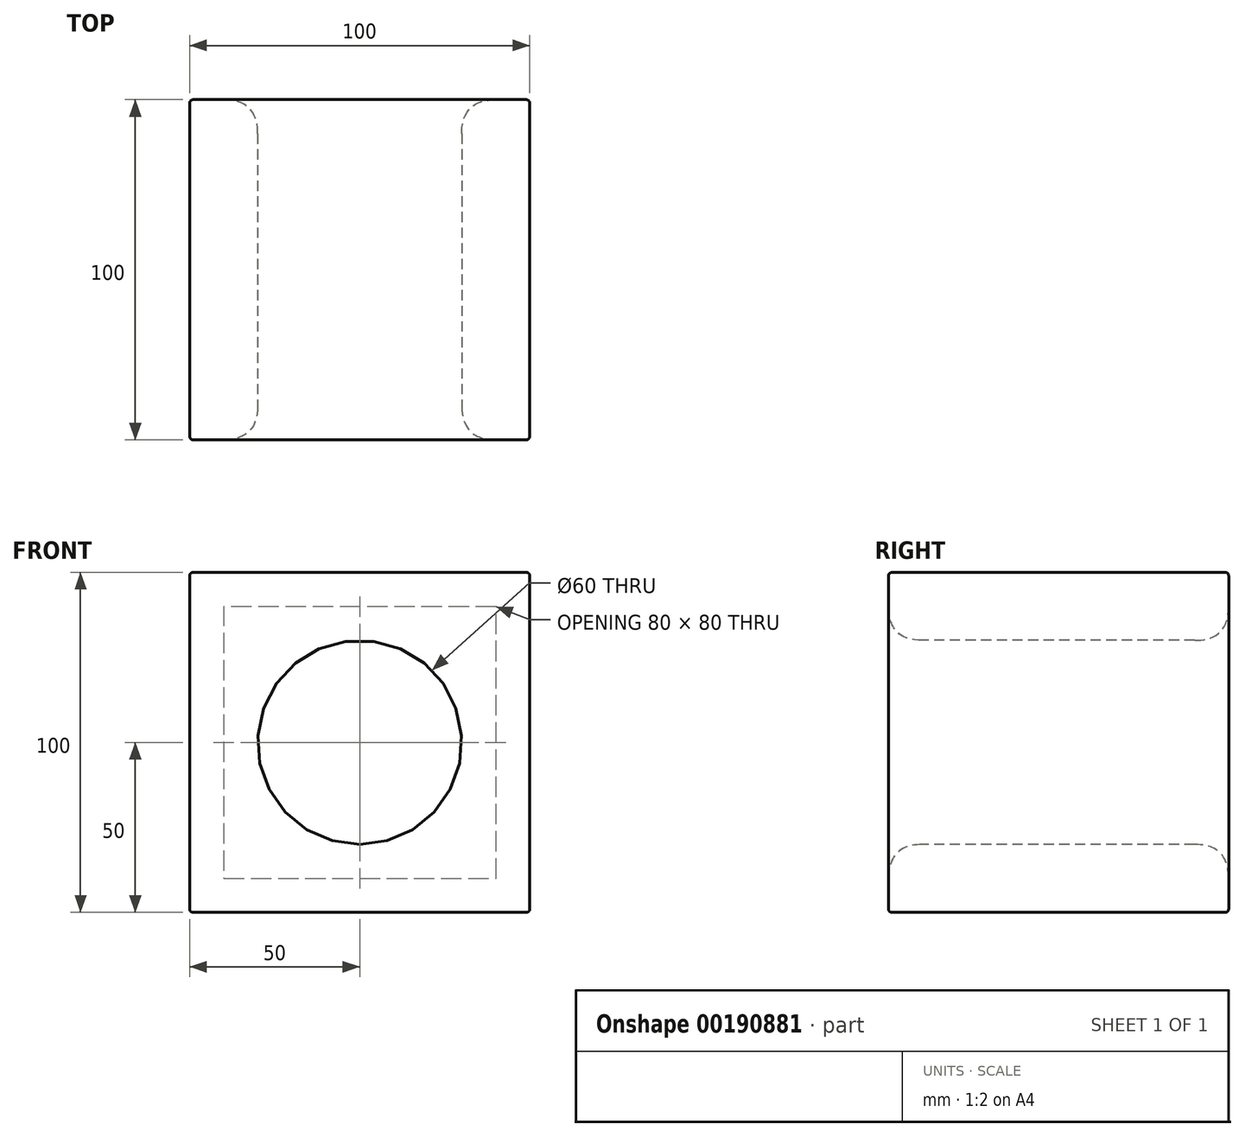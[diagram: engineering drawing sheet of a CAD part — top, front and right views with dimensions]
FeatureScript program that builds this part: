
annotation { "Feature Type Name" : "Feature", "Feature Type Description" : "" }
export const myFeature = defineFeature(function(context is Context, id is Id, definition is map)
    precondition{}
    {
        {
            var Q0;
            Q0=qCreatedBy(makeId("Front.planeOp"),FACE);
            var sketch = newSketch(context, id + "F0", { "sketchPlane" : qUnion([Q0])});
            skLineSegment(sketch, "E0.bottom", {"start": v(50, 50) * mm, "end": v(-50, 50) * mm});
            skLineSegment(sketch, "E0.top", {"start": v(50, -50) * mm, "end": v(-50, -50) * mm});
            skLineSegment(sketch, "E0.left", {"start": v(50, 50) * mm, "end": v(50, -50) * mm});
            skLineSegment(sketch, "E0.right", {"start": v(-50, 50) * mm, "end": v(-50, -50) * mm});
            skPoint(sketch, "E0.middle", {"position": v(0, 0) * mm});
            skSolve(sketch);
        }
        {
            var Q0;
            Q0 = qSketchRegion(id + "F0", true);
            extrude(context, id + "F1", {"entities" : qUnion([Q0]), "depth" : 100 * mm, "symmetric" : true});
        }
        {
            var Q0;
            Q0=makeQuery(id+"F1.opExtrude","CAP_FACE",FACE,{"disambiguationData":[OSD([sQuery(id+"F0.wireOp",EDGE,"E0.bottom"),sQuery(id+"F0.wireOp",EDGE,"E0.top"),sQuery(id+"F0.wireOp",EDGE,"E0.left"),sQuery(id+"F0.wireOp",EDGE,"E0.right")])],"isStart":false});
            var sketch = newSketch(context, id + "F2", { "sketchPlane" : qUnion([Q0])});
            skCircle(sketch, "E1", {"center": v(0, 0) * mm, "radius": 30 * mm});
            skSolve(sketch);
        }
        {
            var Q0;
            Q0 = qSketchRegion(id + "F2", true);
            extrude(context, id + "F3", {"entities" : qUnion([Q0]), "operationType" : NewBodyOperationType.REMOVE, "endBound" : BoundingType.THROUGH_ALL, "oppositeDirection" : true, "depth" : 25 * mm});
        }
        {
            var Q0;
            Q0=makeQuery(id+"F3.boolean.opBoolean","COPY",FACE,{"derivedFrom":makeQuery(id+"F3.opExtrude","SWEPT_FACE",FACE,{"disambiguationData":[OSD([sQuery(id+"F2.wireOp",EDGE,"E1")])]})});
            fillet(context, id + "F4", {"entities" : qUnion([Q0]), "radius" : 10 * mm, "tangentPropagation" : true, "rho" : 0.5, "crossSection" : FilletCrossSection.CONIC, "allowEdgeOverflow" : false});
        }
        {
            var Q0;
            Q0=makeQuery(id+"F1.opExtrude","SWEPT_FACE",FACE,{"disambiguationData":[OSD([sQuery(id+"F0.wireOp",EDGE,"E0.bottom")])]});
            var Q1;
            Q1=makeQuery(id+"F1.opExtrude","SWEPT_FACE",FACE,{"disambiguationData":[OSD([sQuery(id+"F0.wireOp",EDGE,"E0.top")])]});
            var Q2;
            Q2=makeQuery(id+"F1.opExtrude","SWEPT_FACE",FACE,{"disambiguationData":[OSD([sQuery(id+"F0.wireOp",EDGE,"E0.left")])]});
            var Q3;
            Q3=makeQuery(id+"F1.opExtrude","SWEPT_FACE",FACE,{"disambiguationData":[OSD([sQuery(id+"F0.wireOp",EDGE,"E0.right")])]});
            fillet(context, id + "F5", {"entities" : qUnion([Q0, Q1, Q2, Q3]), "radius" : 1 * mm, "tangentPropagation" : true, "allowEdgeOverflow" : false});
        }
    });
